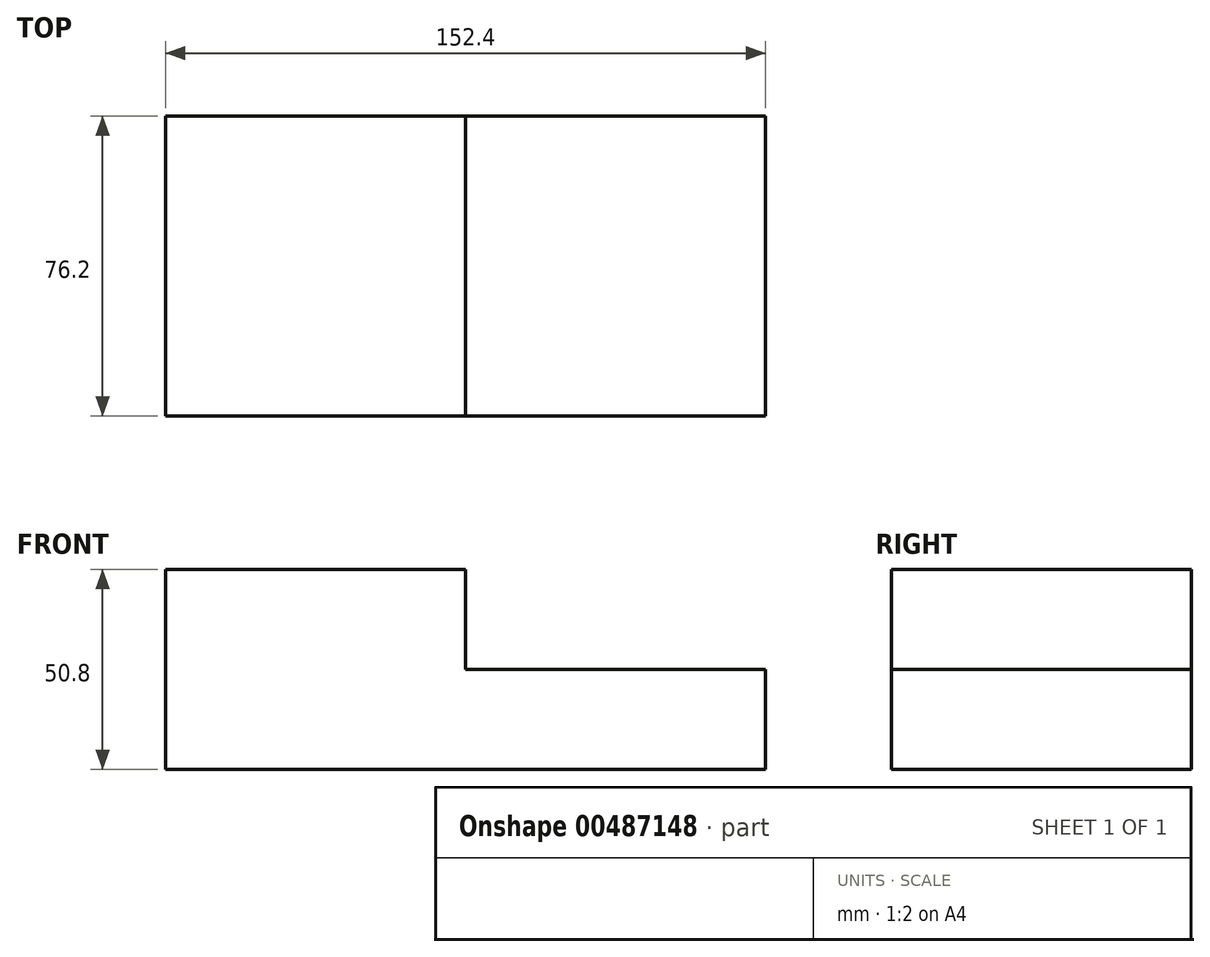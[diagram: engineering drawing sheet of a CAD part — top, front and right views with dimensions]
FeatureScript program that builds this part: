
annotation { "Feature Type Name" : "Feature", "Feature Type Description" : "" }
export const myFeature = defineFeature(function(context is Context, id is Id, definition is map)
    precondition{}
    {
        {
            var Q0;
            Q0=qCreatedBy(makeId("Front.planeOp"),FACE);
            var sketch = newSketch(context, id + "F0", { "sketchPlane" : qUnion([Q0])});
            skLineSegment(sketch, "E0", {"start": v(-101.6, 55.04) * mm, "end": v(-25.4, 55.04) * mm});
            skLineSegment(sketch, "E1", {"start": v(-25.4, 55.04) * mm, "end": v(-25.4, 29.64) * mm});
            skLineSegment(sketch, "E2", {"start": v(-25.4, 29.64) * mm, "end": v(50.8, 29.64) * mm});
            skLineSegment(sketch, "E3", {"start": v(50.8, 29.64) * mm, "end": v(50.8, 4.24) * mm});
            skLineSegment(sketch, "E4", {"start": v(50.8, 4.24) * mm, "end": v(-101.6, 4.24) * mm});
            skLineSegment(sketch, "E5", {"start": v(-101.6, 4.24) * mm, "end": v(-101.6, 55.04) * mm});
            skSolve(sketch);
        }
        {
            var Q0;
            Q0=makeQuery(id+"F0.imprint","IMPRINT",FACE,{"disambiguationData":[TD([[makeQuery(id+"F0.imprint","IMPRINT",EDGE,{"derivedFrom":sQuery(id+"F0.wireOp",EDGE,"E0")}),-1.0]])]});
            extrude(context, id + "F1", {"entities" : qUnion([Q0]), "depth" : 76.2 * mm});
        }
    });
